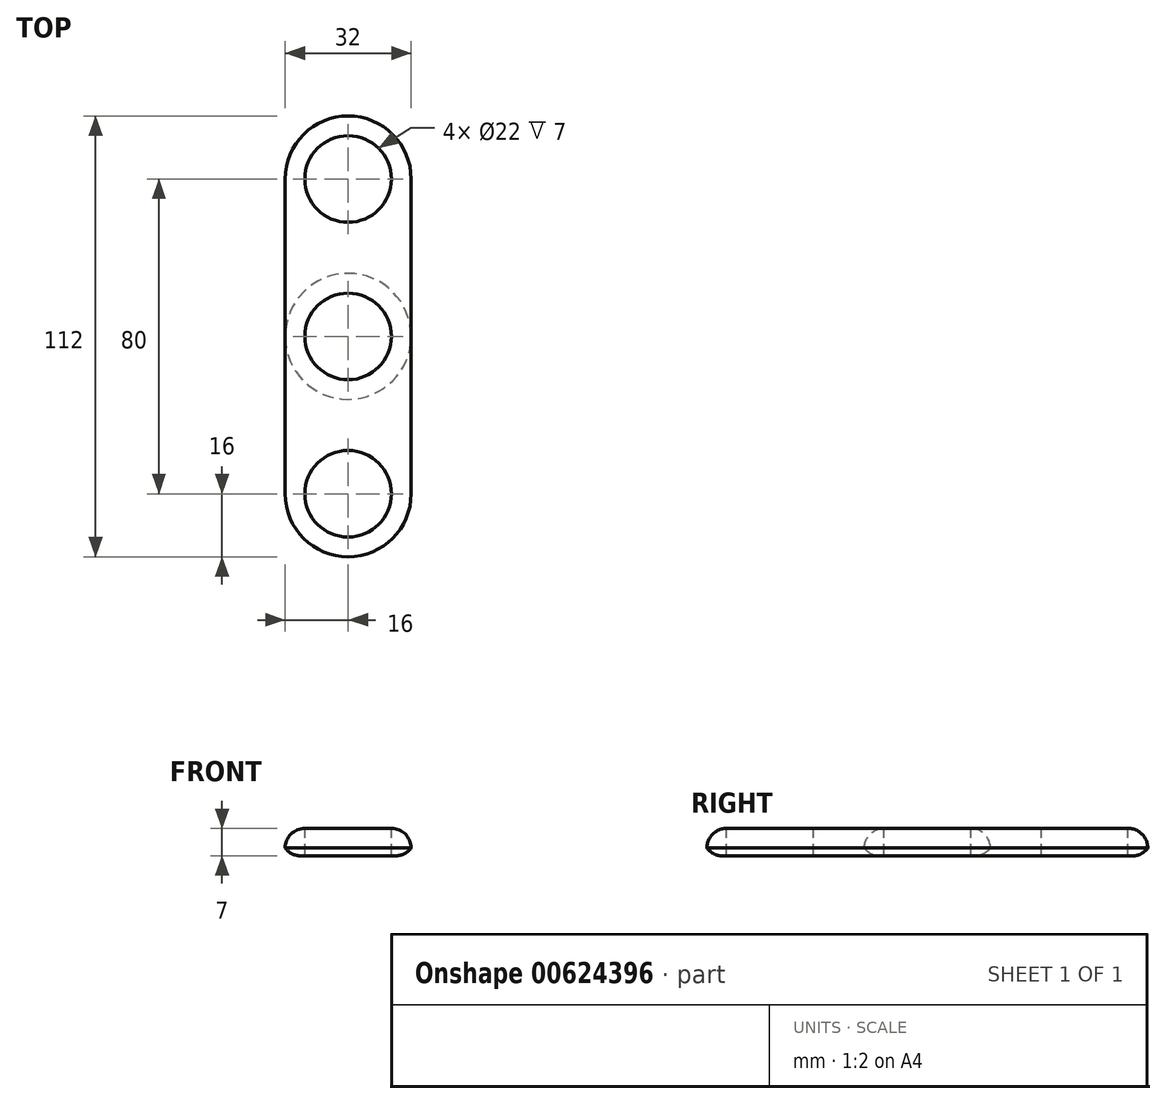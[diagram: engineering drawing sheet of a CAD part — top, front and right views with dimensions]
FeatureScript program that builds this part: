
annotation { "Feature Type Name" : "Feature", "Feature Type Description" : "" }
export const myFeature = defineFeature(function(context is Context, id is Id, definition is map)
    precondition{}
    {
        {
            var Q0;
            Q0=qCreatedBy(makeId("Top.planeOp"),FACE);
            var sketch = newSketch(context, id + "F0", { "sketchPlane" : qUnion([Q0])});
            skCircle(sketch, "E0", {"center": v(0, 0) * mm, "radius": 16 * mm});
            skCircle(sketch, "E1", {"center": v(0, -40) * mm, "radius": 16 * mm});
            skLineSegment(sketch, "E2", {"start": v(-16, 0) * mm, "end": v(-16, -40) * mm});
            skLineSegment(sketch, "E3", {"start": v(16, 0) * mm, "end": v(16, -40) * mm});
            skSolve(sketch);
        }
        {
            var Q0;
            Q0 = qSketchRegion(id + "F0", true);
            extrude(context, id + "F1", {"entities" : qUnion([Q0]), "depth" : 7 * mm, "offsetDistance" : 25 * mm});
        }
        {
            var Q0;
            Q0=makeQuery(id+"F1.opExtrude","CAP_FACE",FACE,{"disambiguationData":[OSD([sQuery(id+"F0.wireOp",EDGE,"E0"),sQuery(id+"F0.wireOp",EDGE,"E1"),sQuery(id+"F0.wireOp",EDGE,"E2"),sQuery(id+"F0.wireOp",EDGE,"E3")])],"isStart":false});
            var sketch = newSketch(context, id + "F2", { "sketchPlane" : qUnion([Q0])});
            skCircle(sketch, "E4", {"center": v(0, 0) * mm, "radius": 11 * mm});
            skCircle(sketch, "E5", {"center": v(0, -40) * mm, "radius": 11 * mm});
            skSolve(sketch);
        }
        {
            var Q0;
            Q0 = qSketchRegion(id + "F2", true);
            extrude(context, id + "F3", {"entities" : qUnion([Q0]), "operationType" : NewBodyOperationType.REMOVE, "endBound" : BoundingType.UP_TO_NEXT, "oppositeDirection" : true, "depth" : 25 * mm, "offsetDistance" : 25 * mm});
        }
        {
            var Q0;
            Q0=qCreatedBy(makeId("Front.planeOp"),FACE);
            var sketch = newSketch(context, id + "F4", { "sketchPlane" : qUnion([Q0])});
            skLineSegment(sketch, "E6", {"start": v(0, 16.49) * mm, "end": v(0, -23.72) * mm});
            skSolve(sketch);
        }
        {
            var Q0;
            Q0=makeQuery(id+"F1.opExtrude","SWEPT_BODY",BODY,{"disambiguationData":[OSD([sQuery(id+"F0.wireOp",EDGE,"E0"),sQuery(id+"F0.wireOp",EDGE,"E1"),sQuery(id+"F0.wireOp",EDGE,"E2"),sQuery(id+"F0.wireOp",EDGE,"E3")])]});
            var Q1;
            Q1=sQuery(id+"F4.wireOp",EDGE,"E6");
            circularPattern(context, id + "F5", {"entities" : qUnion([Q0]), "axis" : qUnion([Q1]), "angle" : 360 * degree, "instanceCount" : 2, "equalSpace" : true});
        }
        {
            var Q0;
            Q0=makeQuery(id+"F1.opExtrude","CAP_EDGE",EDGE,{"disambiguationData":[OSD([sQuery(id+"F0.wireOp",EDGE,"E2")])],"isStart":false});
            var Q1;
            Q1=makeQuery(id+"F5.opPattern","COPY",EDGE,{"derivedFrom":makeQuery(id+"F1.opExtrude","CAP_EDGE",EDGE,{"disambiguationData":[OSD([sQuery(id+"F0.wireOp",EDGE,"E3")])],"isStart":false}),"instanceName":"1"});
            fillet(context, id + "F6", {"entities" : qUnion([Q0, Q1]), "radius" : 5 * mm, "tangentPropagation" : true, "allowEdgeOverflow" : false});
        }
        {
            var Q0;
            Q0=makeQuery(id+"F1.opExtrude","CAP_EDGE",EDGE,{"disambiguationData":[OSD([sQuery(id+"F0.wireOp",EDGE,"E2")])],"isStart":true});
            var Q1;
            Q1=makeQuery(id+"F5.opPattern","COPY",EDGE,{"derivedFrom":makeQuery(id+"F1.opExtrude","CAP_EDGE",EDGE,{"disambiguationData":[OSD([sQuery(id+"F0.wireOp",EDGE,"E3")])],"isStart":true}),"instanceName":"1"});
            fillet(context, id + "F7", {"entities" : qUnion([Q0, Q1]), "radius" : 5 * mm, "tangentPropagation" : true, "allowEdgeOverflow" : false});
        }
    });
